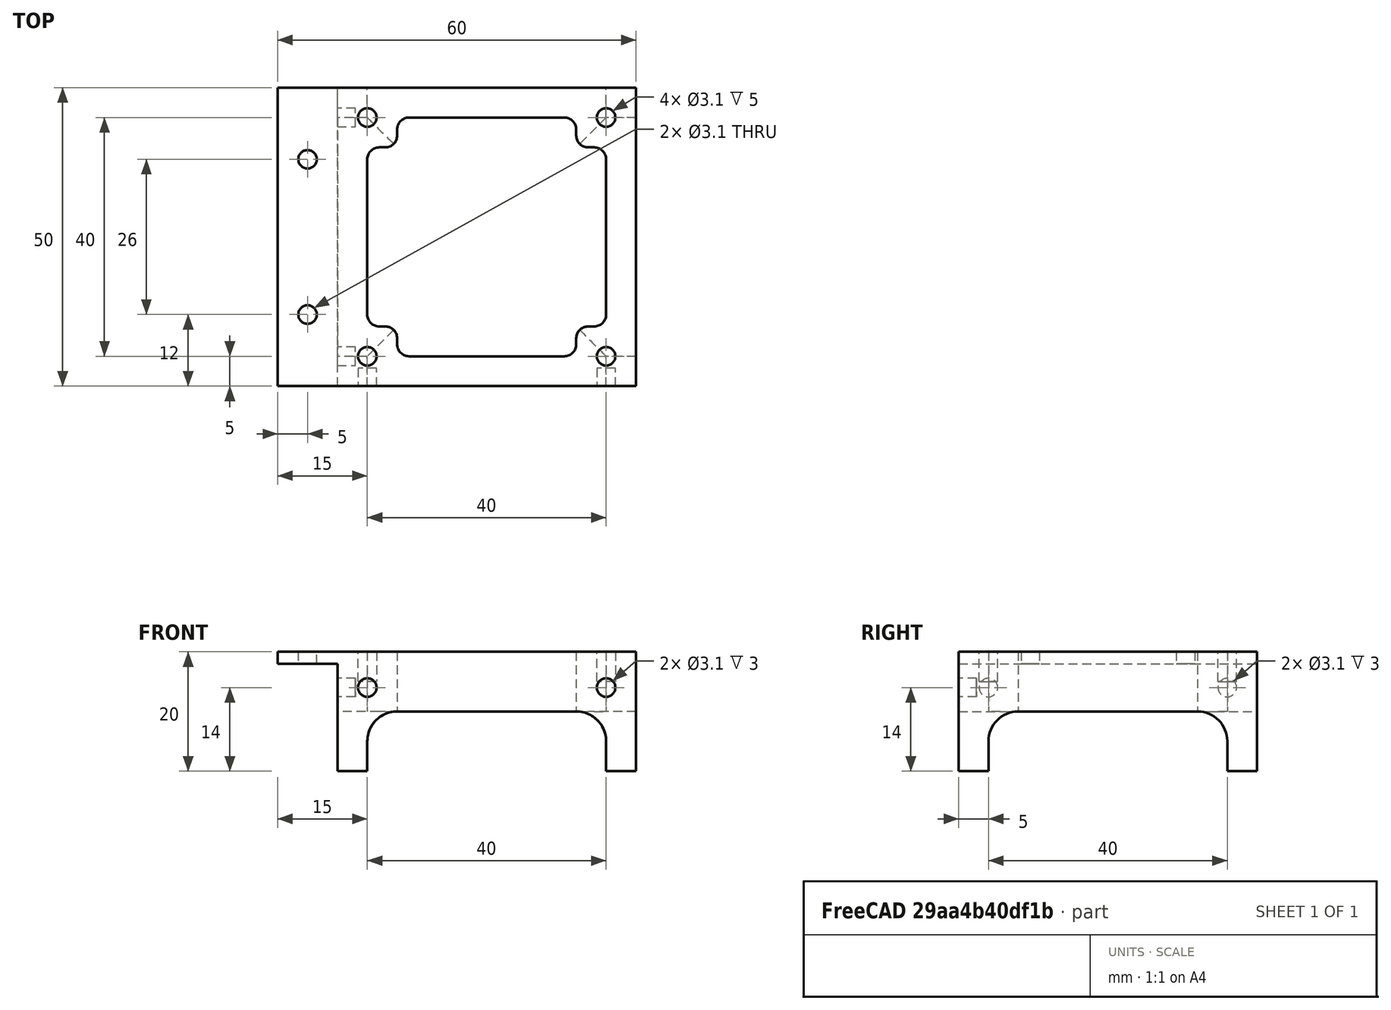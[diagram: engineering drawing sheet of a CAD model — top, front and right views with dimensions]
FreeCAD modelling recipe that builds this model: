
FCSTD DOCUMENT  (FreeCAD 0.20R29603 (Git))
Label: BackplaneBlockTest
License: All rights reserved
LicenseURL: http://en.wikipedia.org/wiki/All_rights_reserved
objects: Sketcher::SketchObject×7, PartDesign::Pocket×6, Part::Cylinder×2, Part::Cut×2, Part::Box×1, PartDesign::Pad×1, PartDesign::Body×1, Part::MultiFuse×1, Mesh::Feature×1
note: 28 computed .brp shape members not serialized (recipe doc carries the construction recipe); baked Part::Feature solids carry a one-line shape summary decoded from their .brp

FEATURE [Part::Box] Box  label="Cube"
  AttacherType = Attacher::AttachEngine3D
  Height = 2
  Length = 10
  Placement = pos=(-10,0,18) rot=(0,0,1;0rad)
  Width = 50
FEATURE [Part::Cylinder] Cylinder
  Angle = 360
  AttacherType = Attacher::AttachEngine3D
  FirstAngle = 0
  Height = 10
  Placement = pos=(-5,12,14) rot=(0,0,1;0rad)
  Radius = 1.55
  SecondAngle = 0
FEATURE [Part::Cut] Cut
  Base = -> Box
  Tool = -> Cylinder
FEATURE [Part::Cylinder] Cylinder001
  Angle = 360
  AttacherType = Attacher::AttachEngine3D
  FirstAngle = 0
  Height = 10
  Placement = pos=(-5,38,14) rot=(0,0,1;0rad)
  Radius = 1.55
  SecondAngle = 0
FEATURE [Part::Cut] Cut001  label="Lip"
  Base = -> Cut
  Tool = -> Cylinder001
FEATURE [Sketcher::SketchObject] Sketch002
  FullyConstrained = true
  MapMode = 5
  Support = -> [XY_Plane002]
  sketch-geometry (4):
    g0: LineSegment StartX=-25 StartY=25 StartZ=0 EndX=25 EndY=25 EndZ=0
    g1: LineSegment StartX=25 StartY=25 StartZ=0 EndX=25 EndY=-25 EndZ=0
    g2: LineSegment StartX=25 StartY=-25 StartZ=0 EndX=-25 EndY=-25 EndZ=0
    g3: LineSegment StartX=-25 StartY=-25 StartZ=0 EndX=-25 EndY=25 EndZ=0
  constraints (10):
    c: Coincident(g0,g1)
    c: Coincident(g1,g2)
    c: Coincident(g2,g3)
    c: Coincident(g3,g0)
    c: Horizontal(g0)
    c: Vertical(g3)
    c: Symmetric(g2,g1,g-2)
    c: Symmetric(g1,g0,g-1)
    c: DistanceY(g1,g1) = 50
    c: DistanceX(g2,g2) = 50
FEATURE [PartDesign::Pad] Pad001
  Direction = (0,0,1)
  Length = 20
  Length2 = 10
  Profile = -> Sketch002
  ReferenceAxis = -> Sketch002 [N_Axis]
  Type = 0
FEATURE [Sketcher::SketchObject] Sketch003
  ExternalGeometry = -> [Pad001]
  FullyConstrained = true
  MapMode = 5
  Placement = pos=(0,0,20) rot=(0,0,1;0rad)
  Support = -> [Pad001]
  sketch-geometry (36):
    g0: LineSegment StartX=-18 StartY=15 StartZ=0 EndX=-17 EndY=15 EndZ=0
    g1: LineSegment StartX=20 StartY=13 StartZ=0 EndX=20 EndY=-13 EndZ=0
    g2: LineSegment StartX=18 StartY=-15 StartZ=0 EndX=17 EndY=-15 EndZ=0
    g3: LineSegment StartX=-20 StartY=-13 StartZ=0 EndX=-20 EndY=13 EndZ=0
    g4: LineSegment StartX=-13 StartY=20 StartZ=0 EndX=13 EndY=20 EndZ=0
    g5: LineSegment StartX=15 StartY=18 StartZ=0 EndX=15 EndY=17 EndZ=0
    g6: LineSegment StartX=13 StartY=-20 StartZ=0 EndX=-13 EndY=-20 EndZ=0
    g7: LineSegment StartX=-15 StartY=-18 StartZ=0 EndX=-15 EndY=-17 EndZ=0
    g8: LineSegment StartX=17 StartY=15 StartZ=0 EndX=18 EndY=15 EndZ=0
    g9: LineSegment StartX=-15 StartY=17 StartZ=0 EndX=-15 EndY=18 EndZ=0
    g10: LineSegment StartX=-17 StartY=-15 StartZ=0 EndX=-18 EndY=-15 EndZ=0
    g11: LineSegment StartX=15 StartY=-17 StartZ=0 EndX=15 EndY=-18 EndZ=0
    g12: ArcOfCircle CenterX=-13 CenterY=-18 CenterZ=0 NormalX=0 NormalY=0 NormalZ=1 AngleXU=0 Radius=2 StartAngle=3.14159 EndAngle=4.71239
    g13: GeomPoint X=-15 Y=-20 Z=0
    g14: ArcOfCircle CenterX=13 CenterY=-18 CenterZ=0 NormalX=0 NormalY=0 NormalZ=1 AngleXU=0 Radius=2 StartAngle=4.71239 EndAngle=6.28319
    g15: GeomPoint X=15 Y=-20 Z=0
    g16: ArcOfCircle CenterX=17 CenterY=-17 CenterZ=0 NormalX=0 NormalY=0 NormalZ=1 AngleXU=0 Radius=2 StartAngle=1.5708 EndAngle=3.14159
    g17: GeomPoint X=15 Y=-15 Z=0
    g18: ArcOfCircle CenterX=18 CenterY=-13 CenterZ=0 NormalX=0 NormalY=0 NormalZ=1 AngleXU=0 Radius=2 StartAngle=4.71239 EndAngle=6.28319
    g19: GeomPoint X=20 Y=-15 Z=0
    g20: ArcOfCircle CenterX=18 CenterY=13 CenterZ=0 NormalX=0 NormalY=0 NormalZ=1 AngleXU=0 Radius=2 StartAngle=0 EndAngle=1.5708
    g21: GeomPoint X=20 Y=15 Z=0
    g22: ArcOfCircle CenterX=17 CenterY=17 CenterZ=0 NormalX=0 NormalY=0 NormalZ=1 AngleXU=0 Radius=2 StartAngle=3.14159 EndAngle=4.71239
    g23: GeomPoint X=15 Y=15 Z=0
    g24: ArcOfCircle CenterX=13 CenterY=18 CenterZ=0 NormalX=0 NormalY=0 NormalZ=1 AngleXU=0 Radius=2 StartAngle=4e-16 EndAngle=1.5708
    g25: GeomPoint X=15 Y=20 Z=0
    g26: ArcOfCircle CenterX=-13 CenterY=18 CenterZ=0 NormalX=0 NormalY=0 NormalZ=1 AngleXU=0 Radius=2 StartAngle=1.5708 EndAngle=3.14159
    g27: GeomPoint X=-15 Y=20 Z=0
    g28: ArcOfCircle CenterX=-17 CenterY=17 CenterZ=0 NormalX=0 NormalY=0 NormalZ=1 AngleXU=0 Radius=2 StartAngle=4.71239 EndAngle=6.28319
    g29: GeomPoint X=-15 Y=15 Z=0
    g30: ArcOfCircle CenterX=-18 CenterY=13 CenterZ=0 NormalX=0 NormalY=0 NormalZ=1 AngleXU=0 Radius=2 StartAngle=1.5708 EndAngle=3.14159
    g31: GeomPoint X=-20 Y=15 Z=0
    g32: ArcOfCircle CenterX=-18 CenterY=-13 CenterZ=0 NormalX=0 NormalY=0 NormalZ=1 AngleXU=0 Radius=2 StartAngle=3.14159 EndAngle=4.71239
    g33: GeomPoint X=-20 Y=-15 Z=0
    g34: ArcOfCircle CenterX=-17 CenterY=-17 CenterZ=0 NormalX=0 NormalY=0 NormalZ=1 AngleXU=0 Radius=2 StartAngle=0 EndAngle=1.5708
    g35: GeomPoint X=-15 Y=-15 Z=0
  constraints (80):
    c: Horizontal(g2)
    c: Vertical(g3)
    c: Symmetric(g21,g31,g-2)
    c: Symmetric(g21,g19,g-1)
    c: DistanceX(g31,g21) = 40
    c: DistanceY(g19,g21) = 30
    c: Horizontal(g4)
    c: Vertical(g7)
    c: Symmetric(g13,g15,g-2)
    c: Symmetric(g15,g25,g-1)
    c: DistanceY(g15,g25) = 40
    c: Vertical(g9)
    c: Vertical(g5)
    c: Vertical(g11)
    c: Horizontal(g10)
    c: Horizontal(g8)
    c: Horizontal(g0)
    c: DistanceX(g13,g15) = 30
    c: DistanceY(g33,g31) = 30
    c: DistanceX(g27,g25) = 30
    c: PointOnObject(g13,g7)
    c: PointOnObject(g13,g6)
    c: Tangent(g7,g12) = 1.5708
    c: Tangent(g6,g12) = 1.5708
    c: Radius(g12) = 2
    c: PointOnObject(g15,g11)
    c: PointOnObject(g15,g6)
    c: Tangent(g11,g14) = 1.5708
    c: Tangent(g6,g14) = 1.5708
    c: PointOnObject(g17,g11)
    c: PointOnObject(g17,g2)
    c: Tangent(g11,g16) = -1.5708
    c: Tangent(g2,g16) = -1.5708
    c: PointOnObject(g19,g2)
    c: PointOnObject(g19,g1)
    c: Tangent(g2,g18) = 1.5708
    c: Tangent(g1,g18) = 1.5708
    c: PointOnObject(g21,g1)
    c: PointOnObject(g21,g8)
    c: Tangent(g1,g20) = 1.5708
    c: Tangent(g8,g20) = 1.5708
    c: PointOnObject(g23,g8)
    c: PointOnObject(g23,g5)
    c: Tangent(g8,g22) = -1.5708
    c: Tangent(g5,g22) = -1.5708
    c: PointOnObject(g25,g5)
    c: PointOnObject(g25,g4)
    c: Tangent(g5,g24) = 1.5708
    c: Tangent(g4,g24) = 1.5708
    c: PointOnObject(g27,g9)
    c: PointOnObject(g27,g4)
    c: Tangent(g9,g26) = 1.5708
    c: Tangent(g4,g26) = 1.5708
    c: PointOnObject(g29,g9)
    c: PointOnObject(g29,g0)
    c: Tangent(g9,g28) = -1.5708
    c: Tangent(g0,g28) = -1.5708
    c: PointOnObject(g31,g0)
    c: PointOnObject(g31,g3)
    c: Tangent(g0,g30) = 1.5708
    c: Tangent(g3,g30) = 1.5708
    c: PointOnObject(g33,g3)
    c: PointOnObject(g33,g10)
    c: Tangent(g3,g32) = 1.5708
    c: Tangent(g10,g32) = 1.5708
    c: PointOnObject(g35,g10)
    c: PointOnObject(g35,g7)
    c: Tangent(g10,g34) = -1.5708
    c: Tangent(g7,g34) = -1.5708
    c: Radius(g34) = 2
    c: Radius(g32) = 2
    c: Radius(g30) = 2
    c: Radius(g28) = 2
    c: Radius(g26) = 2
    c: Radius(g24) = 2
    c: Radius(g22) = 2
    c: Radius(g20) = 2
    c: Radius(g18) = 2
    c: Radius(g16) = 2
    c: Radius(g14) = 2
FEATURE [PartDesign::Pocket] Pocket001
  BaseFeature = -> Pad001
  Direction = (0,0,-1)
  Length = 5
  Length2 = 5
  Profile = -> Sketch003
  ReferenceAxis = -> Sketch003 [N_Axis]
  Type = 1
FEATURE [Sketcher::SketchObject] Sketch004
  ExternalGeometry = -> [Pocket001]
  FullyConstrained = true
  MapMode = 5
  Placement = pos=(25,0,0) rot=(0.57735,0.57735,0.57735;2.0944rad)
  Support = -> [Pocket001]
  sketch-geometry (6):
    g0: LineSegment StartX=-15 StartY=10 StartZ=0 EndX=15 EndY=10 EndZ=0
    g1: LineSegment StartX=20 StartY=5 StartZ=0 EndX=20 EndY=0 EndZ=0
    g2: LineSegment StartX=20 StartY=0 StartZ=0 EndX=-20 EndY=0 EndZ=0
    g3: LineSegment StartX=-20 StartY=0 StartZ=0 EndX=-20 EndY=5 EndZ=0
    g4: ArcOfCircle CenterX=15 CenterY=5 CenterZ=0 NormalX=0 NormalY=0 NormalZ=1 AngleXU=0 Radius=5 StartAngle=1.11001e-11 EndAngle=1.5708
    g5: ArcOfCircle CenterX=-15 CenterY=5 CenterZ=0 NormalX=0 NormalY=0 NormalZ=1 AngleXU=0 Radius=5 StartAngle=1.5708 EndAngle=3.14159
  constraints (15):
    c: Coincident(g1,g2)
    c: Coincident(g2,g3)
    c: Vertical(g1)
    c: Vertical(g3)
    c: PointOnObject(g1,g-1)
    c: Tangent(g1,g4) = 1.5708
    c: Tangent(g0,g4) = 1.5708
    c: Tangent(g0,g5) = 1.5708
    c: Tangent(g3,g5) = 1.5708
    c: Horizontal(g0)
    c: DistanceX(g2,g2) = 40
    c: Symmetric(g2,g1,g-2)
    c: Distance(g-1,g0) = 10
    c: Radius(g5) = 5
    c: Radius(g4) = 5
FEATURE [PartDesign::Pocket] Pocket002
  BaseFeature = -> Pocket001
  Direction = (-1,0,0)
  Length = 5
  Length2 = 5
  Profile = -> Sketch004
  ReferenceAxis = -> Sketch004 [N_Axis]
  Type = 1
FEATURE [Sketcher::SketchObject] Sketch005
  FullyConstrained = true
  MapMode = 5
  Placement = pos=(0,-25,0) rot=(1,0,0;1.5708rad)
  Support = -> [Pocket001]
  sketch-geometry (6):
    g0: LineSegment StartX=-15 StartY=10 StartZ=0 EndX=15 EndY=10 EndZ=0
    g1: LineSegment StartX=20 StartY=5 StartZ=0 EndX=20 EndY=0 EndZ=0
    g2: LineSegment StartX=20 StartY=0 StartZ=0 EndX=-20 EndY=0 EndZ=0
    g3: LineSegment StartX=-20 StartY=0 StartZ=0 EndX=-20 EndY=5 EndZ=0
    g4: ArcOfCircle CenterX=15 CenterY=5 CenterZ=0 NormalX=0 NormalY=0 NormalZ=1 AngleXU=0 Radius=5 StartAngle=1.11e-11 EndAngle=1.5708
    g5: ArcOfCircle CenterX=-15 CenterY=5 CenterZ=0 NormalX=0 NormalY=0 NormalZ=1 AngleXU=0 Radius=5 StartAngle=1.5708 EndAngle=3.14159
  constraints (15):
    c: Coincident(g1,g2)
    c: Coincident(g2,g3)
    c: Horizontal(g0)
    c: Vertical(g1)
    c: Vertical(g3)
    c: Symmetric(g2,g1,g-2)
    c: PointOnObject(g1,g-1)
    c: Tangent(g0,g4) = 1.5708
    c: Tangent(g1,g4) = 1.5708
    c: Tangent(g0,g5) = 1.5708
    c: Tangent(g3,g5) = 1.5708
    c: DistanceX(g2,g2) = 40
    c: Distance(g-1,g0) = 10
    c: Radius(g5) = 5
    c: Radius(g4) = 5
FEATURE [PartDesign::Pocket] Pocket003
  BaseFeature = -> Pocket002
  Direction = (0,1,-2e-16)
  Length = 5
  Length2 = 5
  Profile = -> Sketch005
  ReferenceAxis = -> Sketch005 [N_Axis]
  Type = 1
FEATURE [Sketcher::SketchObject] Sketch009
  FullyConstrained = false
  MapMode = 5
  Placement = pos=(0,0,20) rot=(0,0,1;0rad)
  sketch-geometry (4):
    g0: Circle CenterX=-20 CenterY=20 CenterZ=0 NormalX=0 NormalY=0 NormalZ=1 AngleXU=0 Radius=1.55
    g1: Circle CenterX=20 CenterY=20 CenterZ=0 NormalX=0 NormalY=0 NormalZ=1 AngleXU=0 Radius=1.55
    g2: Circle CenterX=20 CenterY=-20 CenterZ=0 NormalX=0 NormalY=0 NormalZ=1 AngleXU=0 Radius=1.55
    g3: Circle CenterX=-20 CenterY=-20 CenterZ=0 NormalX=0 NormalY=0 NormalZ=1 AngleXU=0 Radius=1.55
  constraints (4):
    c: Diameter(g0) = 3.1
    c: Diameter(g1) = 3.1
    c: Diameter(g2) = 3.1
    c: Diameter(g3) = 3.1
FEATURE [PartDesign::Pocket] Pocket008
  BaseFeature = -> Pocket003
  Direction = (0,0,-1)
  Length = 5
  Length2 = 5
  Profile = -> Sketch009
  ReferenceAxis = -> Sketch009 [N_Axis]
  Type = 0
FEATURE [Sketcher::SketchObject] Sketch015
  ExternalGeometry = -> [Pocket008]
  FullyConstrained = true
  MapMode = 5
  Placement = pos=(0,-25,0) rot=(1,0,0;1.5708rad)
  Support = -> [Pocket008]
  sketch-geometry (2):
    g0: Circle CenterX=-20 CenterY=14 CenterZ=0 NormalX=0 NormalY=0 NormalZ=1 AngleXU=0 Radius=1.55
    g1: Circle CenterX=20 CenterY=14 CenterZ=0 NormalX=0 NormalY=0 NormalZ=1 AngleXU=0 Radius=1.55
  constraints (6):
    c: Diameter(g0) = 3.1
    c: Diameter(g1) = 3.1
    c: Distance(g0,g-5) = 5
    c: Distance(g0,g-3) = 6
    c: Distance(g1,g-3) = 6
    c: Distance(g1,g-4) = 5
FEATURE [PartDesign::Pocket] Pocket013
  BaseFeature = -> Pocket008
  Direction = (0,1,-2e-16)
  Length = 3
  Length2 = 5
  Profile = -> Sketch015
  ReferenceAxis = -> Sketch015 [N_Axis]
  Type = 0
FEATURE [Sketcher::SketchObject] Sketch040
  ExternalGeometry = -> [Pocket013]
  FullyConstrained = true
  MapMode = 5
  Placement = pos=(-25,0,0) rot=(0.57735,-0.57735,-0.57735;2.0944rad)
  Support = -> [Pocket013]
  sketch-geometry (2):
    g0: Circle CenterX=-20 CenterY=14 CenterZ=0 NormalX=0 NormalY=0 NormalZ=1 AngleXU=0 Radius=1.55
    g1: Circle CenterX=20 CenterY=14 CenterZ=0 NormalX=0 NormalY=0 NormalZ=1 AngleXU=0 Radius=1.55
  constraints (6):
    c: Diameter(g0) = 3.1
    c: Diameter(g1) = 3.1
    c: Distance(g0,g-3) = 5
    c: Distance(g0,g-4) = 6
    c: Distance(g1,g-4) = 6
    c: Distance(g1,g-5) = 5
FEATURE [PartDesign::Pocket] Pocket034
  BaseFeature = -> Pocket013
  Direction = (1,0,0)
  Length = 3
  Length2 = 5
  Profile = -> Sketch040
  ReferenceAxis = -> Sketch040 [N_Axis]
  Type = 0
FEATURE [PartDesign::Body] Body002  label="BackplaneBlock"
  Group = -> [Sketch002,Pad001,Sketch003,Pocket001,Sketch004,Sketch005,Pocket002,Pocket003,Sketch009,Pocket008,Sketch015,Pocket013,Sketch040,Pocket034]
  Origin = -> Origin002
  Placement = pos=(25,25,0) rot=(0,0,1;0rad)
  Tip = -> Pocket034
FEATURE [Part::MultiFuse] Fusion
  Shapes = -> [Body002,Cut001]
FEATURE [Mesh::Feature] Mesh  label="Fusion (Meshed)"
